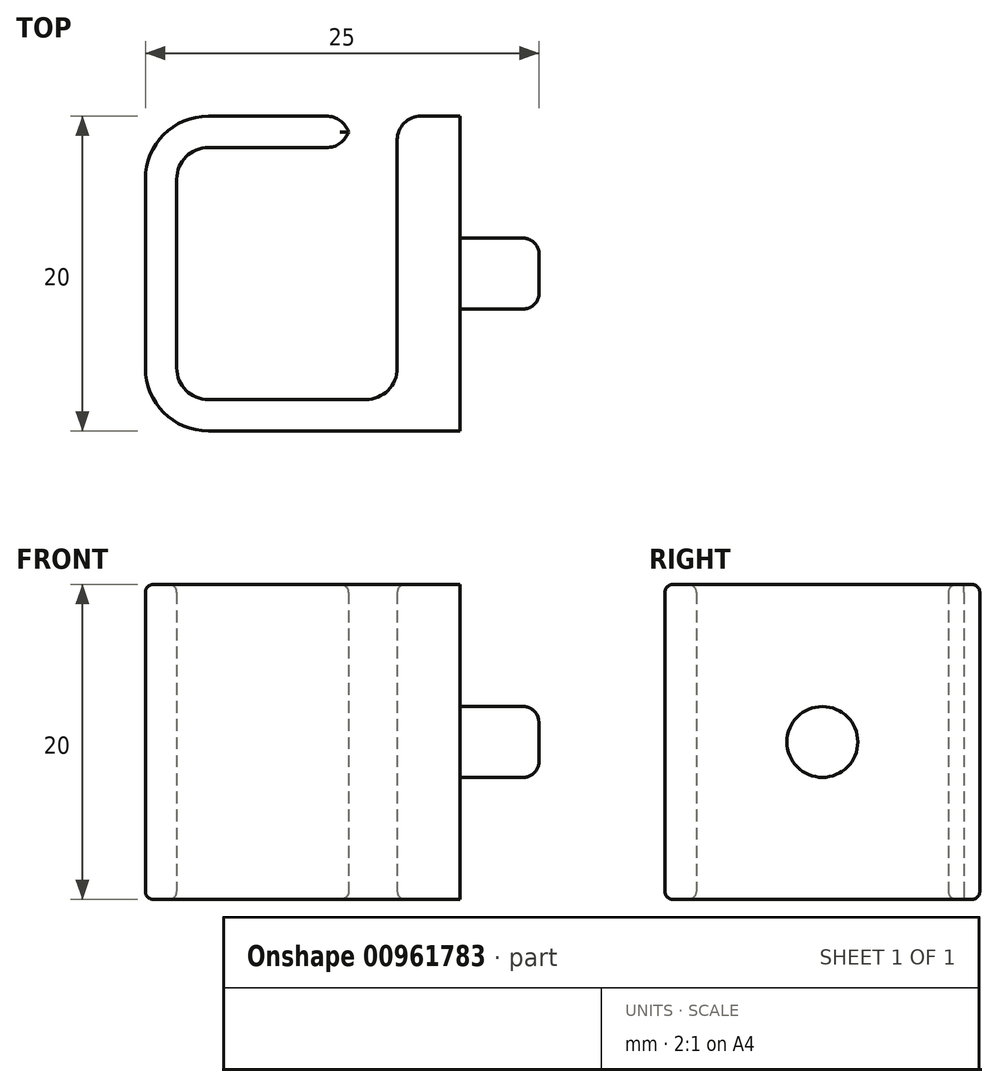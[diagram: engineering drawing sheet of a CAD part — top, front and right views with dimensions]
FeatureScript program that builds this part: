
annotation { "Feature Type Name" : "Feature", "Feature Type Description" : "" }
export const myFeature = defineFeature(function(context is Context, id is Id, definition is map)
    precondition{}
    {
        {
            var Q0;
            Q0=qCreatedBy(makeId("Top.planeOp"),FACE);
            var sketch = newSketch(context, id + "F0", { "sketchPlane" : qUnion([Q0])});
            skLineSegment(sketch, "E0.bottom", {"start": v(10, -10) * mm, "end": v(-6, -10) * mm});
            skLineSegment(sketch, "E0.top", {"start": v(10, 10) * mm, "end": v(7.5, 10) * mm});
            skLineSegment(sketch, "E0.left", {"start": v(10, -10) * mm, "end": v(10, 10) * mm});
            skLineSegment(sketch, "E0.right", {"start": v(-10, -6) * mm, "end": v(-10, 6) * mm});
            skPoint(sketch, "E0.middle", {"position": v(0, 0) * mm});
            skLineSegment(sketch, "E1", {"start": v(-8, 6) * mm, "end": v(-8, -6) * mm});
            skLineSegment(sketch, "E2", {"start": v(-6, -8) * mm, "end": v(4, -8) * mm});
            skLineSegment(sketch, "E3", {"start": v(6, -6) * mm, "end": v(6, 8.5) * mm});
            skLineSegment(sketch, "E4", {"start": v(-6, 8) * mm, "end": v(1.5, 8) * mm});
            skLineSegment(sketch, "E5", {"start": v(3, 8.5) * mm, "end": v(3, 9.5) * mm});
            skPoint(sketch, "E6.orphan", {"position": v(-8, 10) * mm});
            skLineSegment(sketch, "E7.trimOffspring", {"start": v(1.5, 10) * mm, "end": v(-6, 10) * mm});
            skPoint(sketch, "E8.visualSharp", {"position": v(-8, 8) * mm});
            skArc(sketch, "E8.filletArc", {"start": v(-6, 8) * mm, "mid": v(-7.41, 7.41) * mm, "end": v(-8, 6) * mm});
            skPoint(sketch, "E9.visualSharp", {"position": v(-8, -8) * mm});
            skArc(sketch, "E9.filletArc", {"start": v(-8, -6) * mm, "mid": v(-7.41, -7.41) * mm, "end": v(-6, -8) * mm});
            skPoint(sketch, "E10.visualSharp", {"position": v(6, -8) * mm});
            skArc(sketch, "E10.filletArc", {"start": v(4, -8) * mm, "mid": v(5.41, -7.41) * mm, "end": v(6, -6) * mm});
            skPoint(sketch, "E11.visualSharp", {"position": v(3, 10) * mm});
            skArc(sketch, "E11.filletArc", {"start": v(3, 8.5) * mm, "mid": v(2.56, 9.56) * mm, "end": v(1.5, 10) * mm});
            skPoint(sketch, "E12.visualSharp", {"position": v(3, 8) * mm});
            skArc(sketch, "E12.filletArc", {"start": v(1.5, 8) * mm, "mid": v(2.56, 8.44) * mm, "end": v(3, 9.5) * mm});
            skPoint(sketch, "E13.visualSharp", {"position": v(6, 10) * mm});
            skArc(sketch, "E13.filletArc", {"start": v(7.5, 10) * mm, "mid": v(6.44, 9.56) * mm, "end": v(6, 8.5) * mm});
            skPoint(sketch, "E14.visualSharp", {"position": v(-10, 10) * mm});
            skArc(sketch, "E14.filletArc", {"start": v(-6, 10) * mm, "mid": v(-8.83, 8.83) * mm, "end": v(-10, 6) * mm});
            skPoint(sketch, "E15.visualSharp", {"position": v(-10, -10) * mm});
            skArc(sketch, "E15.filletArc", {"start": v(-10, -6) * mm, "mid": v(-8.83, -8.83) * mm, "end": v(-6, -10) * mm});
            skSolve(sketch);
        }
        {
            var Q0;
            Q0=makeQuery(id+"F0.imprint","IMPRINT",FACE,{"disambiguationData":[TD([[makeQuery(id+"F0.imprint","IMPRINT",EDGE,{"derivedFrom":sQuery(id+"F0.wireOp",EDGE,"E0.bottom")}),-1.0]])]});
            extrude(context, id + "F1", {"entities" : qUnion([Q0]), "depth" : 20 * mm, "offsetDistance" : 25 * mm});
        }
        {
            var Q0;
            Q0=makeQuery(id+"F1.opExtrude","SWEPT_FACE",FACE,{"disambiguationData":[OSD([sQuery(id+"F0.wireOp",EDGE,"E0.left")])]});
            var sketch = newSketch(context, id + "F2", { "sketchPlane" : qUnion([Q0])});
            skCircle(sketch, "E16", {"center": v(0, 10) * mm, "radius": 2.25 * mm});
            skPoint(sketch, "E16.centerSnap0", {"position": v(-10, 10) * mm});
            skPoint(sketch, "E16.centerSnap1", {"position": v(0, 20) * mm});
            skSolve(sketch);
        }
        {
            var Q0;
            Q0=makeQuery(id+"F2.imprint","IMPRINT",FACE,{"disambiguationData":[TD([[makeQuery(id+"F2.imprint","IMPRINT",EDGE,{"derivedFrom":sQuery(id+"F2.wireOp",EDGE,"E16")}),1.0]])]});
            extrude(context, id + "F3", {"entities" : qUnion([Q0]), "operationType" : NewBodyOperationType.ADD, "depth" : 5 * mm, "offsetDistance" : 25 * mm});
        }
        {
            var Q0;
            Q0=makeQuery(id+"F3.opExtrude","CAP_EDGE",EDGE,{"disambiguationData":[OSD([sQuery(id+"F2.wireOp",EDGE,"E16")])],"isStart":false});
            var Q1;
            Q1=makeQuery(id+"F3.opExtrude","CAP_EDGE",EDGE,{"disambiguationData":[OSD([sQuery(id+"F2.wireOp",EDGE,"E16")])],"isStart":true});
            fillet(context, id + "F4", {"entities" : qUnion([Q0, Q1]), "radius" : 1 * mm, "tangentPropagation" : true, "allowEdgeOverflow" : false});
        }
        {
            var Q0;
            Q0=makeQuery(id+"F1.opExtrude","CAP_EDGE",EDGE,{"disambiguationData":[OSD([sQuery(id+"F0.wireOp",EDGE,"E1")])],"isStart":false});
            var Q1;
            Q1=makeQuery(id+"F1.opExtrude","CAP_EDGE",EDGE,{"disambiguationData":[OSD([sQuery(id+"F0.wireOp",EDGE,"E1")])],"isStart":true});
            var Q2;
            Q2=makeQuery(id+"F1.opExtrude","CAP_EDGE",EDGE,{"disambiguationData":[OSD([sQuery(id+"F0.wireOp",EDGE,"E0.right")])],"isStart":false});
            var Q3;
            Q3=makeQuery(id+"F1.opExtrude","CAP_EDGE",EDGE,{"disambiguationData":[OSD([sQuery(id+"F0.wireOp",EDGE,"E0.right")])],"isStart":true});
            fillet(context, id + "F5", {"entities" : qUnion([Q0, Q1, Q2, Q3]), "radius" : 0.5 * mm, "tangentPropagation" : true, "allowEdgeOverflow" : false});
        }
    });
